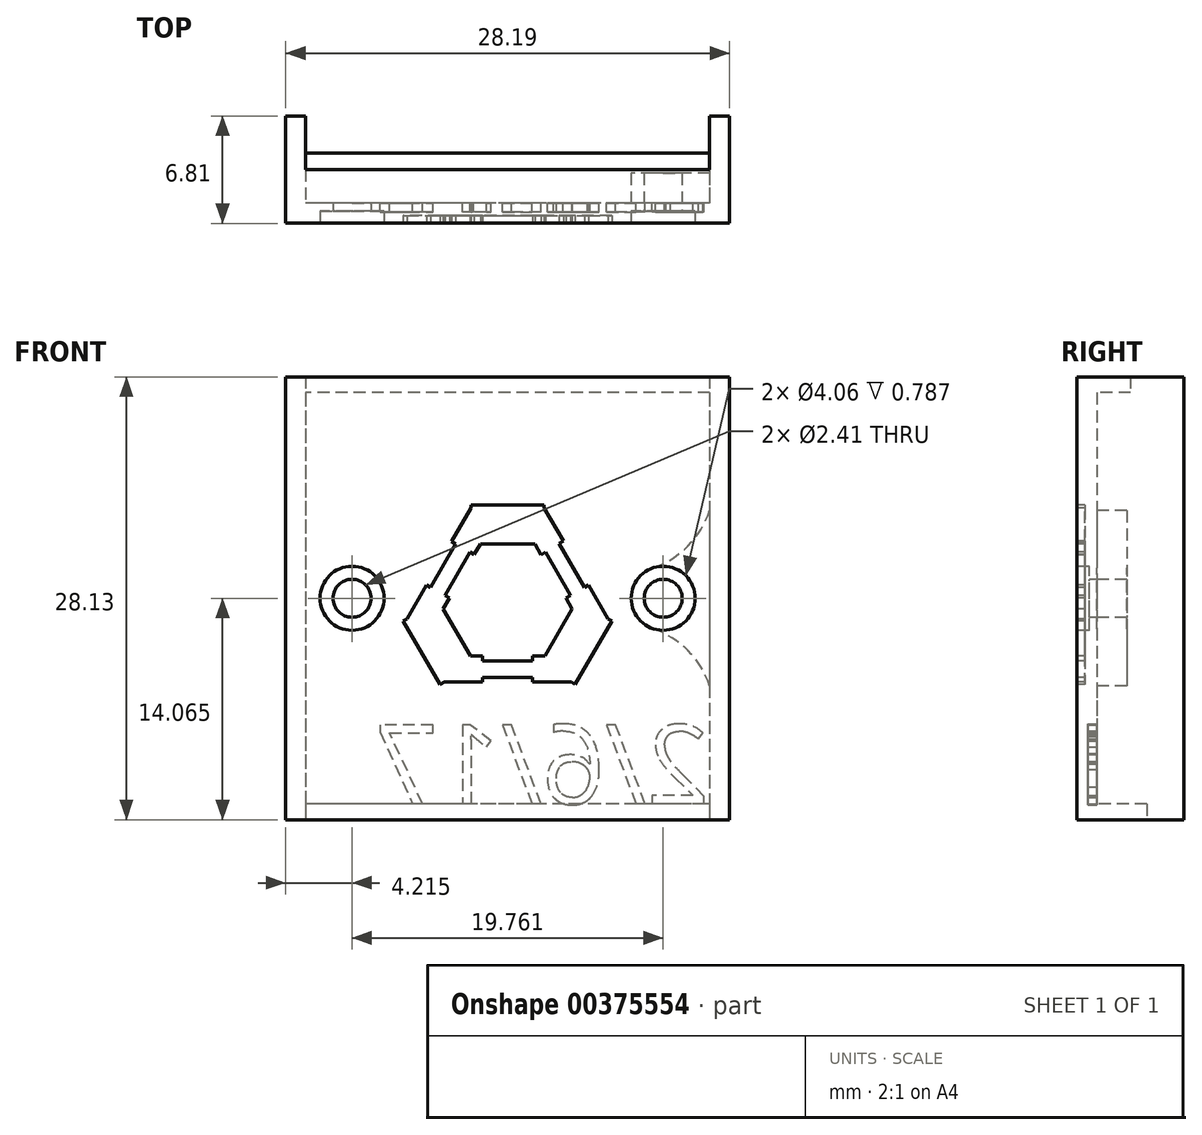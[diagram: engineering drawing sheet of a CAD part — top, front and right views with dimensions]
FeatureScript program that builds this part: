
annotation { "Feature Type Name" : "Feature", "Feature Type Description" : "" }
export const myFeature = defineFeature(function(context is Context, id is Id, definition is map)
    precondition{}
    {
        {
            var Q0;
            Q0=qCreatedBy(makeId("Top.planeOp"),FACE);
            var sketch = newSketch(context, id + "F0", { "sketchPlane" : qUnion([Q0])});
            skLineSegment(sketch, "E0", {"start": v(-22.88, 2.03) * mm, "end": v(-22.88, -1.6) * mm});
            skLineSegment(sketch, "E1", {"start": v(-22.88, -1.6) * mm, "end": v(2.77, -1.6) * mm});
            skLineSegment(sketch, "E2", {"start": v(2.77, -1.6) * mm, "end": v(2.77, 2.03) * mm});
            skLineSegment(sketch, "E3.0", {"start": v(4.04, -2.88) * mm, "end": v(4.04, 2.03) * mm});
            skLineSegment(sketch, "E3.1", {"start": v(-24.15, -2.88) * mm, "end": v(4.04, -2.88) * mm});
            skLineSegment(sketch, "E3.2", {"start": v(-24.15, 2.03) * mm, "end": v(-24.15, -2.88) * mm});
            skLineSegment(sketch, "E4", {"start": v(-24.15, 2.03) * mm, "end": v(-22.88, 2.03) * mm});
            skLineSegment(sketch, "E5", {"start": v(2.77, 2.03) * mm, "end": v(4.04, 2.03) * mm});
            skSolve(sketch);
        }
        {
            var Q0;
            Q0=makeQuery(id+"F0.imprint","IMPRINT",FACE,{"disambiguationData":[TD([[makeQuery(id+"F0.imprint","IMPRINT",EDGE,{"derivedFrom":sQuery(id+"F0.wireOp",EDGE,"E0")}),-1.0]])]});
            extrude(context, id + "F1", {"entities" : qUnion([Q0]), "depth" : 24.13 * mm});
        }
        {
            var Q0;
            Q0=makeQuery(id+"F1.opExtrude","SWEPT_FACE",FACE,{"disambiguationData":[OSD([sQuery(id+"F0.wireOp",EDGE,"E3.1")])]});
            var sketch = newSketch(context, id + "F2", { "sketchPlane" : qUnion([Q0])});
            skLineSegment(sketch, "E6", {"start": v(-10.05, 24.13) * mm, "end": v(-10.05, 0) * mm, "construction": true});
            skLineSegment(sketch, "E7", {"start": v(-19.94, 12.07) * mm, "end": v(-0.17, 12.07) * mm, "construction": true});
            skCircle(sketch, "E8", {"center": v(-19.94, 12.06) * mm, "radius": 2.03 * mm});
            skCircle(sketch, "E9", {"center": v(-0.17, 12.06) * mm, "radius": 2.03 * mm});
            skPoint(sketch, "E10.orphan", {"position": v(-24.15, 12.07) * mm});
            skPoint(sketch, "E11.orphan", {"position": v(4.04, 12.06) * mm});
            skPoint(sketch, "E12", {"position": v(-10.05, 12.06) * mm});
            skCircle(sketch, "E13", {"center": v(-19.94, 12.06) * mm, "radius": 1.2 * mm});
            skCircle(sketch, "E14", {"center": v(-0.17, 12.06) * mm, "radius": 1.2 * mm});
            skSolve(sketch);
        }
        {
            var Q0;
            Q0=makeQuery(id+"F2.imprint","IMPRINT",FACE,{"disambiguationData":[TD([[makeQuery(id+"F2.imprint","IMPRINT",EDGE,{"derivedFrom":sQuery(id+"F2.wireOp",EDGE,"E8")}),1.0]])]});
            var Q1;
            Q1=makeQuery(id+"F2.imprint","IMPRINT",FACE,{"disambiguationData":[TD([[makeQuery(id+"F2.imprint","IMPRINT",EDGE,{"derivedFrom":sQuery(id+"F2.wireOp",EDGE,"E9")}),1.0]])]});
            extrude(context, id + "F3", {"entities" : qUnion([Q0, Q1]), "operationType" : NewBodyOperationType.REMOVE, "oppositeDirection" : true, "depth" : 0.79 * mm});
        }
        {
            var Q0;
            Q0=makeQuery(id+"F3.boolean.opBoolean","SPLIT",FACE,{"disambiguationData":[TD([makeQuery(id+"F3.opExtrude","SWEPT_FACE",FACE,{"disambiguationData":[OSD([sQuery(id+"F2.wireOp",EDGE,"E13")])]})])],"derivedFrom":makeQuery(id+"F1.opExtrude","SWEPT_FACE",FACE,{"disambiguationData":[OSD([sQuery(id+"F0.wireOp",EDGE,"E3.1")])]})});
            var Q1;
            Q1=makeQuery(id+"F3.boolean.opBoolean","SPLIT",FACE,{"disambiguationData":[TD([makeQuery(id+"F3.opExtrude","SWEPT_FACE",FACE,{"disambiguationData":[OSD([sQuery(id+"F2.wireOp",EDGE,"E14")])]})])],"derivedFrom":makeQuery(id+"F1.opExtrude","SWEPT_FACE",FACE,{"disambiguationData":[OSD([sQuery(id+"F0.wireOp",EDGE,"E3.1")])]})});
            extrude(context, id + "F4", {"entities" : qUnion([Q0, Q1]), "operationType" : NewBodyOperationType.REMOVE, "oppositeDirection" : true, "depth" : 25.4 * mm});
        }
        {
            var Q0;
            {var subQ0=sQuery(id+"F0.wireOp",EDGE,"E3.0");var subQ4=sQuery(id+"F0.wireOp",EDGE,"E3.1");Q0=makeQuery(id+"F3.boolean.opBoolean","SPLIT",FACE,{"disambiguationData":[TD([makeQuery(id+"F1.opExtrude","SWEPT_FACE",FACE,{"disambiguationData":[OSD([subQ0])]})])],"derivedFrom":makeQuery(id+"F1.opExtrude","SWEPT_FACE",FACE,{"disambiguationData":[OSD([subQ4])]})});}
            var sketch = newSketch(context, id + "F5", { "sketchPlane" : qUnion([Q0])});
            skLineSegment(sketch, "E15", {"start": v(-10.05, 24.13) * mm, "end": v(-10.05, 0) * mm, "construction": true});
            skPoint(sketch, "E16", {"position": v(-10.05, 6.37) * mm});
            skLineSegment(sketch, "E17", {"start": v(-13.6, 15.68) * mm, "end": v(-12.4, 17.81) * mm});
            skLineSegment(sketch, "E18", {"start": v(-12.4, 17.81) * mm, "end": v(-12.4, 17.97) * mm});
            skLineSegment(sketch, "E19", {"start": v(-12.4, 17.97) * mm, "end": v(-7.74, 17.97) * mm});
            skLineSegment(sketch, "E20", {"start": v(-7.74, 17.97) * mm, "end": v(-7.74, 17.81) * mm});
            skLineSegment(sketch, "E21", {"start": v(-7.74, 17.81) * mm, "end": v(-6.51, 15.7) * mm});
            skLineSegment(sketch, "E22", {"start": v(-6.51, 15.7) * mm, "end": v(-6.78, 15.53) * mm});
            skLineSegment(sketch, "E23", {"start": v(-6.78, 15.53) * mm, "end": v(-5.18, 12.76) * mm});
            skLineSegment(sketch, "E24", {"start": v(-5.18, 12.76) * mm, "end": v(-4.92, 12.91) * mm});
            skLineSegment(sketch, "E25", {"start": v(-4.92, 12.91) * mm, "end": v(-3.68, 10.76) * mm});
            skLineSegment(sketch, "E26", {"start": v(-3.68, 10.76) * mm, "end": v(-3.44, 10.64) * mm});
            skLineSegment(sketch, "E27", {"start": v(-3.44, 10.64) * mm, "end": v(-5.76, 6.6) * mm});
            skLineSegment(sketch, "E28", {"start": v(-5.76, 6.6) * mm, "end": v(-6, 6.74) * mm});
            skLineSegment(sketch, "E29", {"start": v(-6, 6.74) * mm, "end": v(-8.47, 6.74) * mm});
            skLineSegment(sketch, "E30", {"start": v(-8.47, 6.74) * mm, "end": v(-8.47, 7.04) * mm});
            skLineSegment(sketch, "E31", {"start": v(-8.47, 7.04) * mm, "end": v(-11.65, 7.04) * mm});
            skLineSegment(sketch, "E32", {"start": v(-11.65, 7.04) * mm, "end": v(-11.65, 6.74) * mm});
            skLineSegment(sketch, "E33", {"start": v(-11.65, 6.74) * mm, "end": v(-14.07, 6.74) * mm});
            skLineSegment(sketch, "E34", {"start": v(-14.07, 6.74) * mm, "end": v(-14.35, 6.58) * mm});
            skLineSegment(sketch, "E35", {"start": v(-14.35, 6.58) * mm, "end": v(-16.68, 10.62) * mm});
            skLineSegment(sketch, "E36", {"start": v(-16.68, 10.62) * mm, "end": v(-16.45, 10.76) * mm});
            skLineSegment(sketch, "E37", {"start": v(-16.45, 10.76) * mm, "end": v(-15.22, 12.91) * mm});
            skLineSegment(sketch, "E38", {"start": v(-15.22, 12.91) * mm, "end": v(-14.94, 12.76) * mm});
            skLineSegment(sketch, "E39", {"start": v(-14.94, 12.76) * mm, "end": v(-13.35, 15.53) * mm});
            skLineSegment(sketch, "E40", {"start": v(-13.35, 15.53) * mm, "end": v(-13.6, 15.68) * mm});
            skLineSegment(sketch, "E41", {"start": v(-11.79, 15.5) * mm, "end": v(-8.33, 15.5) * mm});
            skLineSegment(sketch, "E42", {"start": v(-8.33, 15.5) * mm, "end": v(-7.94, 14.83) * mm});
            skLineSegment(sketch, "E43", {"start": v(-7.94, 14.83) * mm, "end": v(-7.65, 15) * mm});
            skLineSegment(sketch, "E44", {"start": v(-7.65, 15) * mm, "end": v(-6.06, 12.25) * mm});
            skLineSegment(sketch, "E45", {"start": v(-6.06, 12.25) * mm, "end": v(-6.36, 12.07) * mm});
            skLineSegment(sketch, "E46", {"start": v(-6.36, 12.07) * mm, "end": v(-5.97, 11.4) * mm});
            skLineSegment(sketch, "E47", {"start": v(-5.97, 11.4) * mm, "end": v(-7.69, 8.4) * mm});
            skLineSegment(sketch, "E48", {"start": v(-7.69, 8.4) * mm, "end": v(-8.47, 8.4) * mm});
            skLineSegment(sketch, "E49", {"start": v(-8.47, 8.4) * mm, "end": v(-8.47, 8.08) * mm});
            skLineSegment(sketch, "E50", {"start": v(-8.47, 8.08) * mm, "end": v(-11.64, 8.08) * mm});
            skLineSegment(sketch, "E51", {"start": v(-11.64, 8.08) * mm, "end": v(-11.64, 8.39) * mm});
            skLineSegment(sketch, "E52", {"start": v(-11.64, 8.39) * mm, "end": v(-12.41, 8.39) * mm});
            skLineSegment(sketch, "E53", {"start": v(-12.41, 8.39) * mm, "end": v(-14.15, 11.39) * mm});
            skLineSegment(sketch, "E54", {"start": v(-14.15, 11.39) * mm, "end": v(-13.76, 12.07) * mm});
            skLineSegment(sketch, "E55", {"start": v(-13.76, 12.07) * mm, "end": v(-14.04, 12.23) * mm});
            skLineSegment(sketch, "E56", {"start": v(-14.04, 12.23) * mm, "end": v(-12.46, 15) * mm});
            skLineSegment(sketch, "E57", {"start": v(-12.46, 15) * mm, "end": v(-12.18, 14.84) * mm});
            skLineSegment(sketch, "E58", {"start": v(-12.18, 14.84) * mm, "end": v(-11.79, 15.5) * mm});
            skSolve(sketch);
        }
        {
            var Q0;
            Q0=makeQuery(id+"F5.imprint","IMPRINT",FACE,{"disambiguationData":[TD([[makeQuery(id+"F5.imprint","IMPRINT",EDGE,{"derivedFrom":sQuery(id+"F5.wireOp",EDGE,"E17")}),-1.0]])]});
            extrude(context, id + "F6", {"entities" : qUnion([Q0]), "operationType" : NewBodyOperationType.REMOVE, "oppositeDirection" : true, "depth" : .5 * mm});
        }
        {
            var Q0;
            Q0=makeQuery(id+"F1.opExtrude","CAP_FACE",FACE,{"disambiguationData":[OSD([sQuery(id+"F0.wireOp",EDGE,"E0"),sQuery(id+"F0.wireOp",EDGE,"E1"),sQuery(id+"F0.wireOp",EDGE,"E2"),sQuery(id+"F0.wireOp",EDGE,"E3.0"),sQuery(id+"F0.wireOp",EDGE,"E3.1"),sQuery(id+"F0.wireOp",EDGE,"E3.2"),sQuery(id+"F0.wireOp",EDGE,"E4"),sQuery(id+"F0.wireOp",EDGE,"E5")])],"isStart":true});
            extrude(context, id + "F7", {"entities" : qUnion([Q0]), "operationType" : NewBodyOperationType.ADD, "depth" : 2 * mm});
        }
        {
            var Q0;
            Q0=makeQuery(id+"F1.opExtrude","CAP_FACE",FACE,{"disambiguationData":[OSD([sQuery(id+"F0.wireOp",EDGE,"E0"),sQuery(id+"F0.wireOp",EDGE,"E1"),sQuery(id+"F0.wireOp",EDGE,"E2"),sQuery(id+"F0.wireOp",EDGE,"E3.0"),sQuery(id+"F0.wireOp",EDGE,"E3.1"),sQuery(id+"F0.wireOp",EDGE,"E3.2"),sQuery(id+"F0.wireOp",EDGE,"E4"),sQuery(id+"F0.wireOp",EDGE,"E5")])],"isStart":false});
            extrude(context, id + "F8", {"entities" : qUnion([Q0]), "operationType" : NewBodyOperationType.ADD, "depth" : 2 * mm});
        }
        {
            var Q0;
            {var subQ0=sQuery(id+"F0.wireOp",EDGE,"E1");Q0=makeQuery(id+"F8.boolean.opBoolean","MERGE",FACE,{"derivedFrom":[makeQuery(id+"F7.boolean.opBoolean","MERGE",FACE,{"derivedFrom":[makeQuery(id+"F1.opExtrude","SWEPT_FACE",FACE,{"disambiguationData":[OSD([subQ0])]}),makeQuery(id+"F7.opExtrude","SWEPT_FACE",FACE,{"disambiguationData":[OSD([subQ0])]})]}),makeQuery(id+"F8.opExtrude","SWEPT_FACE",FACE,{"disambiguationData":[OSD([subQ0])]})]});}
            var sketch = newSketch(context, id + "F9", { "sketchPlane" : qUnion([Q0])});
            skLineSegment(sketch, "E59.top", {"start": v(-2.77, 24.13) * mm, "end": v(22.88, 24.13) * mm, "construction": true});
            skLineSegment(sketch, "E59.left", {"start": v(-2.77, 26.13) * mm, "end": v(-2.77, 24.13) * mm, "construction": true});
            skLineSegment(sketch, "E59.right", {"start": v(22.88, 26.13) * mm, "end": v(22.88, 24.13) * mm, "construction": true});
            skLineSegment(sketch, "E60.bottom", {"start": v(-2.77, 26.13) * mm, "end": v(22.88, 26.13) * mm});
            skLineSegment(sketch, "E60.top", {"start": v(-2.77, 25.13) * mm, "end": v(22.88, 25.13) * mm});
            skLineSegment(sketch, "E60.left", {"start": v(-2.77, 26.13) * mm, "end": v(-2.77, 25.13) * mm});
            skLineSegment(sketch, "E60.right", {"start": v(22.88, 26.13) * mm, "end": v(22.88, 25.13) * mm});
            skLineSegment(sketch, "E61", {"start": v(-2.77, 12.07) * mm, "end": v(7.16, 12.07) * mm, "construction": true});
            skLineSegment(sketch, "E62.MirrorCS", {"start": v(-2.77, -1) * mm, "end": v(22.88, -1) * mm});
            skLineSegment(sketch, "E63.MirrorCS", {"start": v(-2.77, -2) * mm, "end": v(22.88, -2) * mm});
            skLineSegment(sketch, "E64", {"start": v(-2.77, -1) * mm, "end": v(-2.77, -2) * mm});
            skLineSegment(sketch, "E65", {"start": v(22.88, -1) * mm, "end": v(22.88, -2) * mm});
            skSolve(sketch);
        }
        {
            var Q0;
            Q0=makeQuery(id+"F9.imprint","IMPRINT",FACE,{"disambiguationData":[TD([[makeQuery(id+"F9.imprint","IMPRINT",EDGE,{"derivedFrom":sQuery(id+"F9.wireOp",EDGE,"E60.bottom")}),1.0]])]});
            var Q1;
            Q1=makeQuery(id+"F9.imprint","IMPRINT",FACE,{"disambiguationData":[TD([[makeQuery(id+"F9.imprint","IMPRINT",EDGE,{"derivedFrom":sQuery(id+"F9.wireOp",EDGE,"E62.MirrorCS")}),-1.0]])]});
            extrude(context, id + "F10", {"entities" : qUnion([Q0, Q1]), "operationType" : NewBodyOperationType.ADD, "depth" : 1.27 * mm});
        }
        {
            var Q0;
            {var subQ0=sQuery(id+"F0.wireOp",EDGE,"E1");Q0=makeQuery(id+"F8.boolean.opBoolean","MERGE",FACE,{"derivedFrom":[makeQuery(id+"F7.boolean.opBoolean","MERGE",FACE,{"derivedFrom":[makeQuery(id+"F1.opExtrude","SWEPT_FACE",FACE,{"disambiguationData":[OSD([subQ0])]}),makeQuery(id+"F7.opExtrude","SWEPT_FACE",FACE,{"disambiguationData":[OSD([subQ0])]})]}),makeQuery(id+"F8.opExtrude","SWEPT_FACE",FACE,{"disambiguationData":[OSD([subQ0])]})]});}
            var sketch = newSketch(context, id + "F11", { "sketchPlane" : qUnion([Q0])});
            skLineSegment(sketch, "E66", {"start": v(20.32, 12.06) * mm, "end": v(19.81, 12.06) * mm, "construction": true});
            skLineSegment(sketch, "E67", {"start": v(10.05, -1) * mm, "end": v(10.05, 25.13) * mm, "construction": true});
            skArc(sketch, "E68.0", {"start": v(0.83, 10.13) * mm, "mid": v(2.22, 12.06) * mm, "end": v(0.83, 14) * mm});
            skArc(sketch, "E69", {"start": v(-2.77, 17.63) * mm, "mid": v(-1.4, 15.4) * mm, "end": v(0.83, 14) * mm});
            skLineSegment(sketch, "E70", {"start": v(0.17, 12.06) * mm, "end": v(0, 12.06) * mm, "construction": true});
            skArc(sketch, "E71.MirrorCS", {"start": v(-2.77, 6.5) * mm, "mid": v(-1.4, 8.74) * mm, "end": v(0.83, 10.13) * mm});
            skArc(sketch, "E72.MirrorCS", {"start": v(22.88, 17.63) * mm, "mid": v(21.51, 15.4) * mm, "end": v(19.28, 14) * mm});
            skArc(sketch, "E73.MirrorCS", {"start": v(19.28, 10.13) * mm, "mid": v(17.9, 12.07) * mm, "end": v(19.28, 14) * mm});
            skArc(sketch, "E74.MirrorCS", {"start": v(22.88, 6.5) * mm, "mid": v(21.51, 8.74) * mm, "end": v(19.28, 10.13) * mm});
            skLineSegment(sketch, "E75", {"start": v(-2.77, 17.63) * mm, "end": v(-2.77, 6.5) * mm});
            skLineSegment(sketch, "E76", {"start": v(22.88, 17.63) * mm, "end": v(22.88, 6.5) * mm});
            skLineSegment(sketch, "E77", {"start": v(-2.77, 17.63) * mm, "end": v(-2.77, 25.13) * mm});
            skLineSegment(sketch, "E78", {"start": v(-2.77, 25.13) * mm, "end": v(22.88, 25.13) * mm});
            skLineSegment(sketch, "E79", {"start": v(22.88, 25.13) * mm, "end": v(22.88, 17.63) * mm});
            skLineSegment(sketch, "E80", {"start": v(22.88, 6.5) * mm, "end": v(22.88, -1) * mm});
            skLineSegment(sketch, "E81", {"start": v(22.88, -1) * mm, "end": v(-2.77, -1) * mm});
            skLineSegment(sketch, "E82", {"start": v(-2.77, -1) * mm, "end": v(-2.77, 6.5) * mm});
            skCircle(sketch, "E83.0", {"center": v(0.17, 12.06) * mm, "radius": 1.2 * mm});
            skCircle(sketch, "E83.1", {"center": v(19.94, 12.06) * mm, "radius": 1.2 * mm});
            skSolve(sketch);
        }
        {
            var Q0;
            Q0=makeQuery(id+"F11.imprint","IMPRINT",FACE,{"disambiguationData":[TD([[makeQuery(id+"F11.imprint","IMPRINT",EDGE,{"derivedFrom":sQuery(id+"F11.wireOp",EDGE,"5b848598-8b62-4473-9078-29c7f42ded91.0")}),1.0]])]});
            var Q1;
            Q1=makeQuery(id+"F11.imprint","IMPRINT",FACE,{"disambiguationData":[TD([[makeQuery(id+"F11.imprint","IMPRINT",EDGE,{"derivedFrom":sQuery(id+"F11.wireOp",EDGE,"292e60b4-9bbb-43bc-9e86-de80fa0e97c2.0")}),1.0]])]});
            var Q2;
            Q2=makeQuery(id+"F11.imprint","IMPRINT",FACE,{"disambiguationData":[TD([[makeQuery(id+"F11.imprint","IMPRINT",EDGE,{"derivedFrom":sQuery(id+"F11.wireOp",EDGE,"E68.0")}),1.0]])]});
            var Q3;
            Q3=makeQuery(id+"F11.imprint","IMPRINT",FACE,{"disambiguationData":[TD([[makeQuery(id+"F11.imprint","IMPRINT",EDGE,{"derivedFrom":sQuery(id+"F11.wireOp",EDGE,"E72.MirrorCS")}),1.0]])]});
            extrude(context, id + "F12", {"entities" : qUnion([Q0, Q1, Q2, Q3]), "operationType" : NewBodyOperationType.ADD, "depth" : 1.9 * mm});
        }
        {
            var Q0;
            {var subQ0=sQuery(id+"F0.wireOp",EDGE,"E4");Q0=makeQuery(id+"F8.boolean.opBoolean","MERGE",FACE,{"derivedFrom":[makeQuery(id+"F7.boolean.opBoolean","MERGE",FACE,{"derivedFrom":[makeQuery(id+"F1.opExtrude","SWEPT_FACE",FACE,{"disambiguationData":[OSD([subQ0])]}),makeQuery(id+"F7.opExtrude","SWEPT_FACE",FACE,{"disambiguationData":[OSD([subQ0])]})]}),makeQuery(id+"F8.opExtrude","SWEPT_FACE",FACE,{"disambiguationData":[OSD([subQ0])]})]});}
            var Q1;
            Q1=makeQuery(id+"F10.opExtrude","CAP_FACE",FACE,{"disambiguationData":[OSD([sQuery(id+"F9.wireOp",EDGE,"E60.bottom"),sQuery(id+"F9.wireOp",EDGE,"E60.top"),sQuery(id+"F9.wireOp",EDGE,"E60.left"),sQuery(id+"F9.wireOp",EDGE,"E60.right")])],"isStart":false});
            var Q2;
            Q2=makeQuery(id+"F10.opExtrude","CAP_FACE",FACE,{"disambiguationData":[OSD([sQuery(id+"F9.wireOp",EDGE,"E62.MirrorCS"),sQuery(id+"F9.wireOp",EDGE,"E64"),sQuery(id+"F9.wireOp",EDGE,"E63.MirrorCS"),sQuery(id+"F9.wireOp",EDGE,"E65")])],"isStart":false});
            var Q3;
            {var subQ0=sQuery(id+"F0.wireOp",EDGE,"E5");Q3=makeQuery(id+"F8.boolean.opBoolean","MERGE",FACE,{"derivedFrom":[makeQuery(id+"F7.boolean.opBoolean","MERGE",FACE,{"derivedFrom":[makeQuery(id+"F1.opExtrude","SWEPT_FACE",FACE,{"disambiguationData":[OSD([subQ0])]}),makeQuery(id+"F7.opExtrude","SWEPT_FACE",FACE,{"disambiguationData":[OSD([subQ0])]})]}),makeQuery(id+"F8.opExtrude","SWEPT_FACE",FACE,{"disambiguationData":[OSD([subQ0])]})]});}
            extrude(context, id + "F13", {"entities" : qUnion([Q0, Q1, Q2, Q3]), "operationType" : NewBodyOperationType.ADD, "depth" : 1.9 * mm});
        }
        {
            var Q0;
            Q0=makeQuery(id+"F13.opExtrude","CAP_FACE",FACE,{"disambiguationData":[OSD([sQuery(id+"F9.wireOp",EDGE,"E60.bottom"),sQuery(id+"F9.wireOp",EDGE,"E60.top"),sQuery(id+"F9.wireOp",EDGE,"E60.left"),sQuery(id+"F9.wireOp",EDGE,"E60.right")])],"isStart":false});
            extrude(context, id + "F14", {"entities" : qUnion([Q0]), "operationType" : NewBodyOperationType.REMOVE, "oppositeDirection" : true, "depth" : 1.04 * mm});
        }
        {
            var Q0;
            {var subQ0=sQuery(id+"F0.wireOp",EDGE,"E1");Q0=makeQuery(id+"F8.boolean.opBoolean","MERGE",FACE,{"derivedFrom":[makeQuery(id+"F7.boolean.opBoolean","MERGE",FACE,{"derivedFrom":[makeQuery(id+"F1.opExtrude","SWEPT_FACE",FACE,{"disambiguationData":[OSD([subQ0])]}),makeQuery(id+"F7.opExtrude","SWEPT_FACE",FACE,{"disambiguationData":[OSD([subQ0])]})]}),makeQuery(id+"F8.opExtrude","SWEPT_FACE",FACE,{"disambiguationData":[OSD([subQ0])]})]});}
            var sketch = newSketch(context, id + "F15", { "sketchPlane" : qUnion([Q0])});
            skText(sketch, "E84", { "text": "2/6/17", "fontName": "OpenSans-Regular.ttf"});
            const initialGuessF15  = {"E84": [-0.00277, -0.001, 1, 0, 0.00507]};
            skSetInitialGuess(sketch, initialGuessF15);
            skSolve(sketch);
        }
        {
            var Q0;
            Q0 = qSketchRegion(id + "F15", true);
            extrude(context, id + "F16", {"entities" : qUnion([Q0]), "operationType" : NewBodyOperationType.REMOVE, "oppositeDirection" : true, "depth" : 0.56 * mm});
        }
    });
